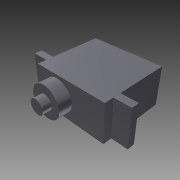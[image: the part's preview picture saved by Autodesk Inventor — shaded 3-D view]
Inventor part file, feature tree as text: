
AUTODESK INVENTOR PART (.ipt)
format: ipt  version: 2014 (Build 180170000, 170)  size: 103,936 bytes
history: native  units: mm
features: extrude x3, sketch x3, other x1
ambient origin geometry x8: Origin, YZ Plane, XZ Plane, XY Plane, X Axis, Y Axis, Z Axis, Center Point
bodies: Body1 (feature_tree)
feature tree (7):
  other  "Sólido1"
  extrude  "Extrusión1"  Depth=21.0mm
  extrude  "Extrusión2"  Depth=10.0mm
  extrude  "Extrusión3"  Depth=4.0mm TaperAngle=0.0deg
  sketch  "Boceto1"  dims[d0=23.0mm d1=21.0mm]
  sketch  "Boceto2"  dims[d2=12.0mm d3=0.0mm d4=10.0mm]
  sketch  "Boceto3"  dims[d5=7.5mm d6=4.0mm d7=0.0mm d8=5.0mm d9=2.3mm d10=5.0mm d11=2.3mm d12=4.66mm d13=2.7mm d14=0.0mm]
